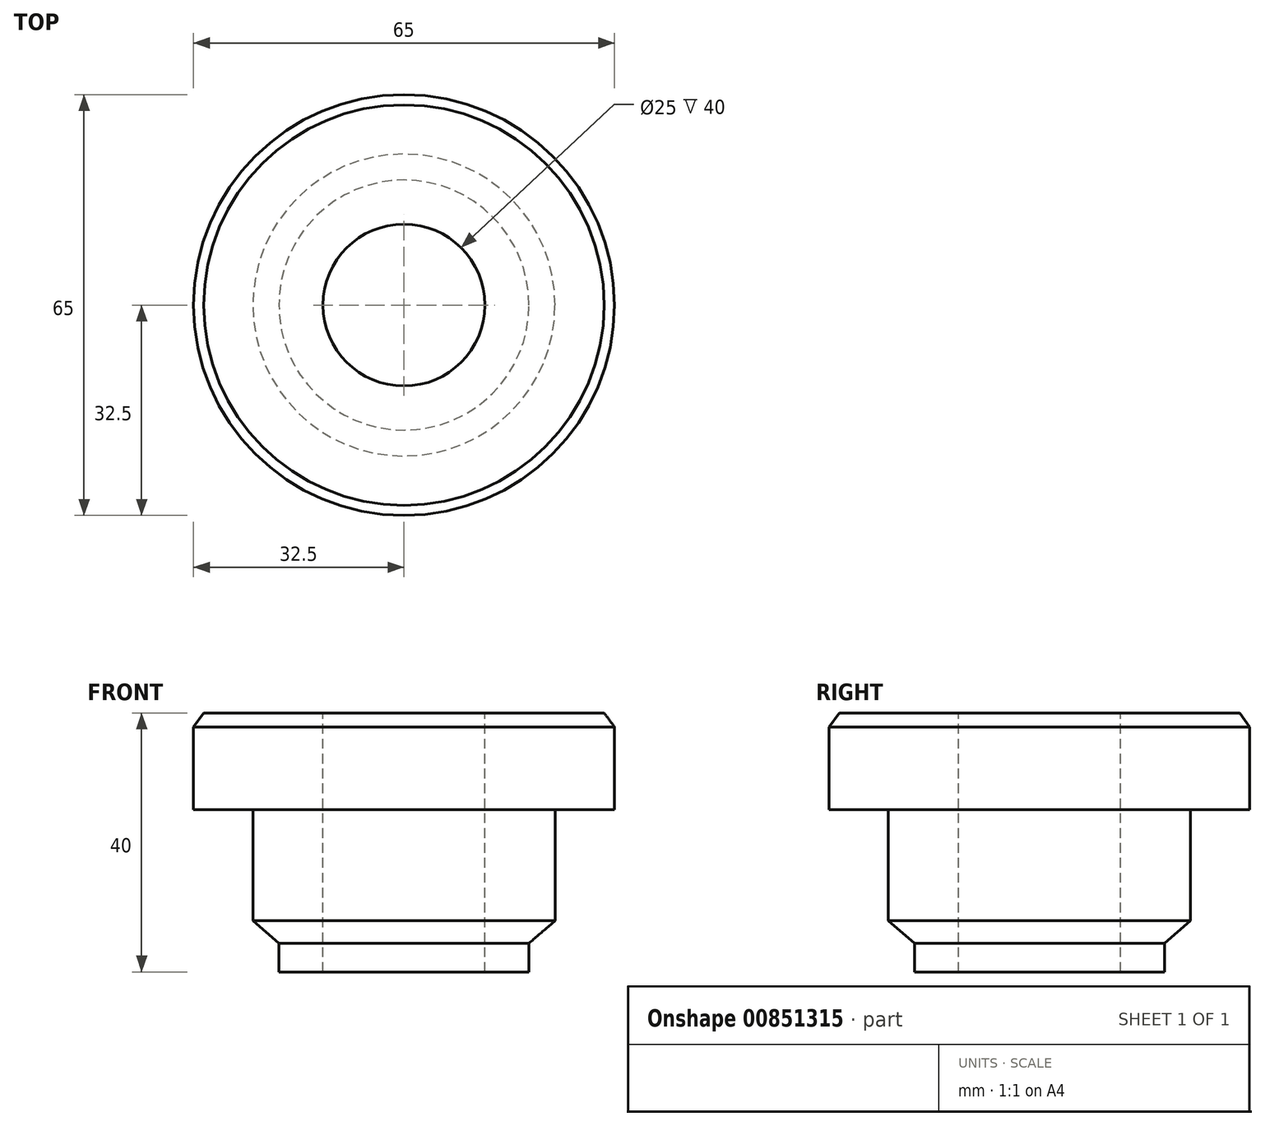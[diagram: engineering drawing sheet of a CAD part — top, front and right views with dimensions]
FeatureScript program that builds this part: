
annotation { "Feature Type Name" : "Feature", "Feature Type Description" : "" }
export const myFeature = defineFeature(function(context is Context, id is Id, definition is map)
    precondition{}
    {
        {
            var Q0;
            Q0=qCreatedBy(makeId("Front.planeOp"),FACE);
            var sketch = newSketch(context, id + "F0", { "sketchPlane" : qUnion([Q0])});
            skLineSegment(sketch, "E0", {"start": v(0, 0) * mm, "end": v(0, 4.44) * mm});
            skLineSegment(sketch, "E1", {"start": v(0, 4.44) * mm, "end": v(4.01, 7.89) * mm});
            skLineSegment(sketch, "E2", {"start": v(4.01, 7.89) * mm, "end": v(4.01, 25.09) * mm});
            skLineSegment(sketch, "E3", {"start": v(4.01, 25.09) * mm, "end": v(13.19, 25.09) * mm});
            skLineSegment(sketch, "E4", {"start": v(13.19, 25.09) * mm, "end": v(13.19, 37.85) * mm});
            skLineSegment(sketch, "E5", {"start": v(13.19, 37.85) * mm, "end": v(11.61, 40) * mm});
            skLineSegment(sketch, "E6", {"start": v(11.61, 40) * mm, "end": v(-19.31, 40) * mm});
            skLineSegment(sketch, "E7", {"start": v(-19.31, 40) * mm, "end": v(-19.31, 0) * mm});
            skLineSegment(sketch, "E8", {"start": v(-19.31, 0) * mm, "end": v(0, 0) * mm});
            skSolve(sketch);
        }
        {
            var Q0;
            Q0=makeQuery(id+"F0.imprint","IMPRINT",FACE,{"disambiguationData":[TD([[makeQuery(id+"F0.imprint","IMPRINT",EDGE,{"derivedFrom":sQuery(id+"F0.wireOp",EDGE,"E0")}),1.0]])]});
            var Q1;
            Q1=sQuery(id+"F0.wireOp",EDGE,"E7");
            revolve(context, id + "F1", {"surfaceOperationType" : NewSurfaceOperationType.NEW, "entities" : qUnion([Q0]), "axis" : qUnion([Q1]), "revolveType" : RevolveType.FULL});
        }
        {
            var Q0;
            Q0=makeQuery(id+"F1.opRevolve","SWEPT_FACE",FACE,{"disambiguationData":[OSD([sQuery(id+"F0.wireOp",EDGE,"E6")])]});
            var sketch = newSketch(context, id + "F2", { "sketchPlane" : qUnion([Q0])});
            skCircle(sketch, "E9", {"center": v(-19.31, 0) * mm, "radius": 12.5 * mm});
            skSolve(sketch);
        }
        {
            var Q0;
            Q0 = qSketchRegion(id + "F2", true);
            extrude(context, id + "F3", {"entities" : qUnion([Q0]), "operationType" : NewBodyOperationType.REMOVE, "endBound" : BoundingType.THROUGH_ALL, "oppositeDirection" : true, "depth" : 25 * mm, "offsetDistance" : 25 * mm});
        }
    });
